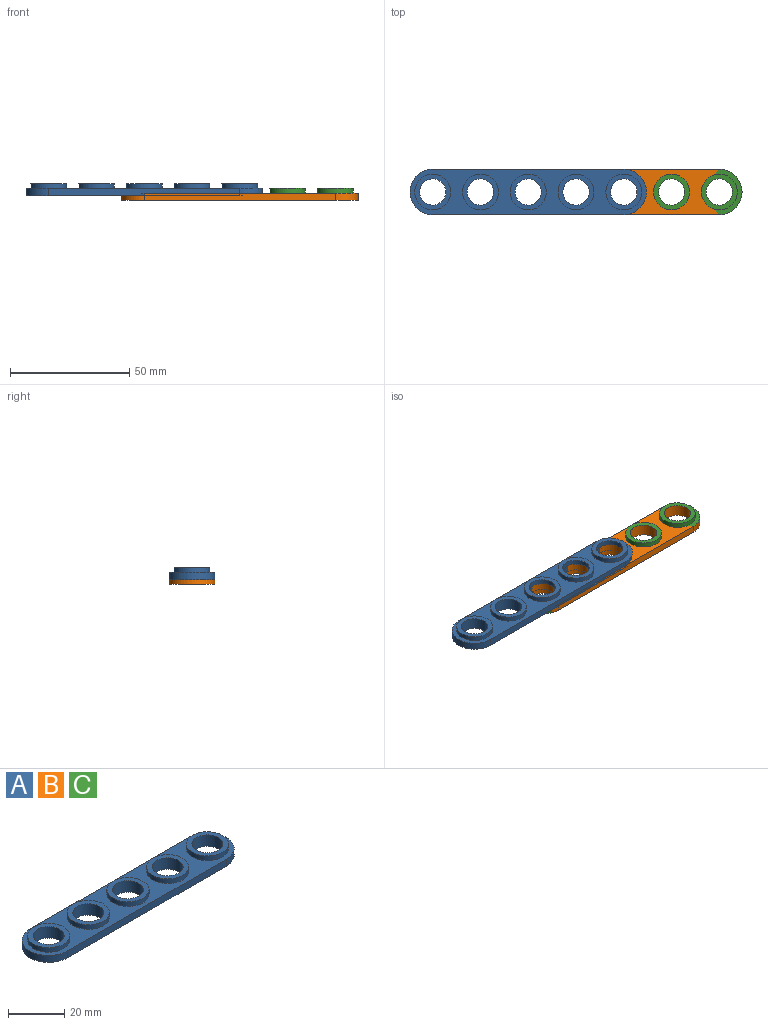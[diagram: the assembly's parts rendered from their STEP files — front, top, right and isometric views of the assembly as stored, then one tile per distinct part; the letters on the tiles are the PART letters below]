
ASSEMBLY  parts=3 mates=1
PART A: 21 faces, bbox 99x19x5 mm
  f0: cylinder r=9.5mm len=19mm, axis (0,0,-1), area 89.5mm2, adj f1,f7,f9,f10
  f1: plane 80x3mm, normal (0,1,0), area 240mm2, adj f0,f2,f9,f10
  f2: cylinder r=9.5mm len=19mm, axis (0,0,-1), area 89.5mm2, adj f1,f7,f9,f10
  f3: cylinder r=5.5mm len=11mm, axis (0,0,-1), area 172.8mm2, adj f10,f18
  f4: cylinder r=5.5mm len=11mm, axis (0,0,-1), area 172.8mm2, adj f10,f16
  f5: cylinder r=5.5mm len=11mm, axis (0,0,-1), area 172.8mm2, adj f10,f14
  f6: cylinder r=5.5mm len=11mm, axis (0,0,-1), area 172.8mm2, adj f10,f12
  f7: plane 80x3mm, normal (0,-1,0), area 240mm2, adj f0,f2,f9,f10
  f8: cylinder r=5.5mm len=11mm, axis (0,0,-1), area 172.8mm2, adj f10,f20
  f9: plane 99x19mm, normal (0,0,1), area 920mm2, adj f0,f1,f2,f7,f11,f13,f15,f17
  f10: plane 99x19mm, normal (0,0,-1), area 1328.4mm2, adj f0,f1,f2,f3,f4,f5,f6,f7
  f11: cylinder r=7.5mm len=15mm, axis (0,0,-1), area 94.2mm2, adj f9,f12
  f12: plane 15x15mm, normal (0,0,1), area 81.7mm2, adj f6,f11
  f13: cylinder r=7.5mm len=15mm, axis (0,0,-1), area 94.2mm2, adj f9,f14
  f14: plane 15x15mm, normal (0,0,1), area 81.7mm2, adj f5,f13
  f15: cylinder r=7.5mm len=15mm, axis (0,0,-1), area 94.2mm2, adj f9,f16
  f16: plane 15x15mm, normal (0,0,1), area 81.7mm2, adj f4,f15
  f17: cylinder r=7.5mm len=15mm, axis (0,0,-1), area 94.2mm2, adj f9,f18
  f18: plane 15x15mm, normal (0,0,1), area 81.7mm2, adj f3,f17
  f19: cylinder r=7.5mm len=15mm, axis (0,0,-1), area 94.2mm2, adj f9,f20
  f20: plane 15x15mm, normal (0,0,1), area 81.7mm2, adj f8,f19
PART B: same geometry as A
PART C: same geometry as A
PLACE A t=(-55.17,-42.71,5.7)mm
PLACE B t=(-15.17,-42.71,3.7)mm
PLACE C t=(-15.17,-42.71,3.7)mm fixed
MATE slider C.f2 <-> A.f4  axis (0,0,1) through (-104.67,-33.21,8.7)mm
